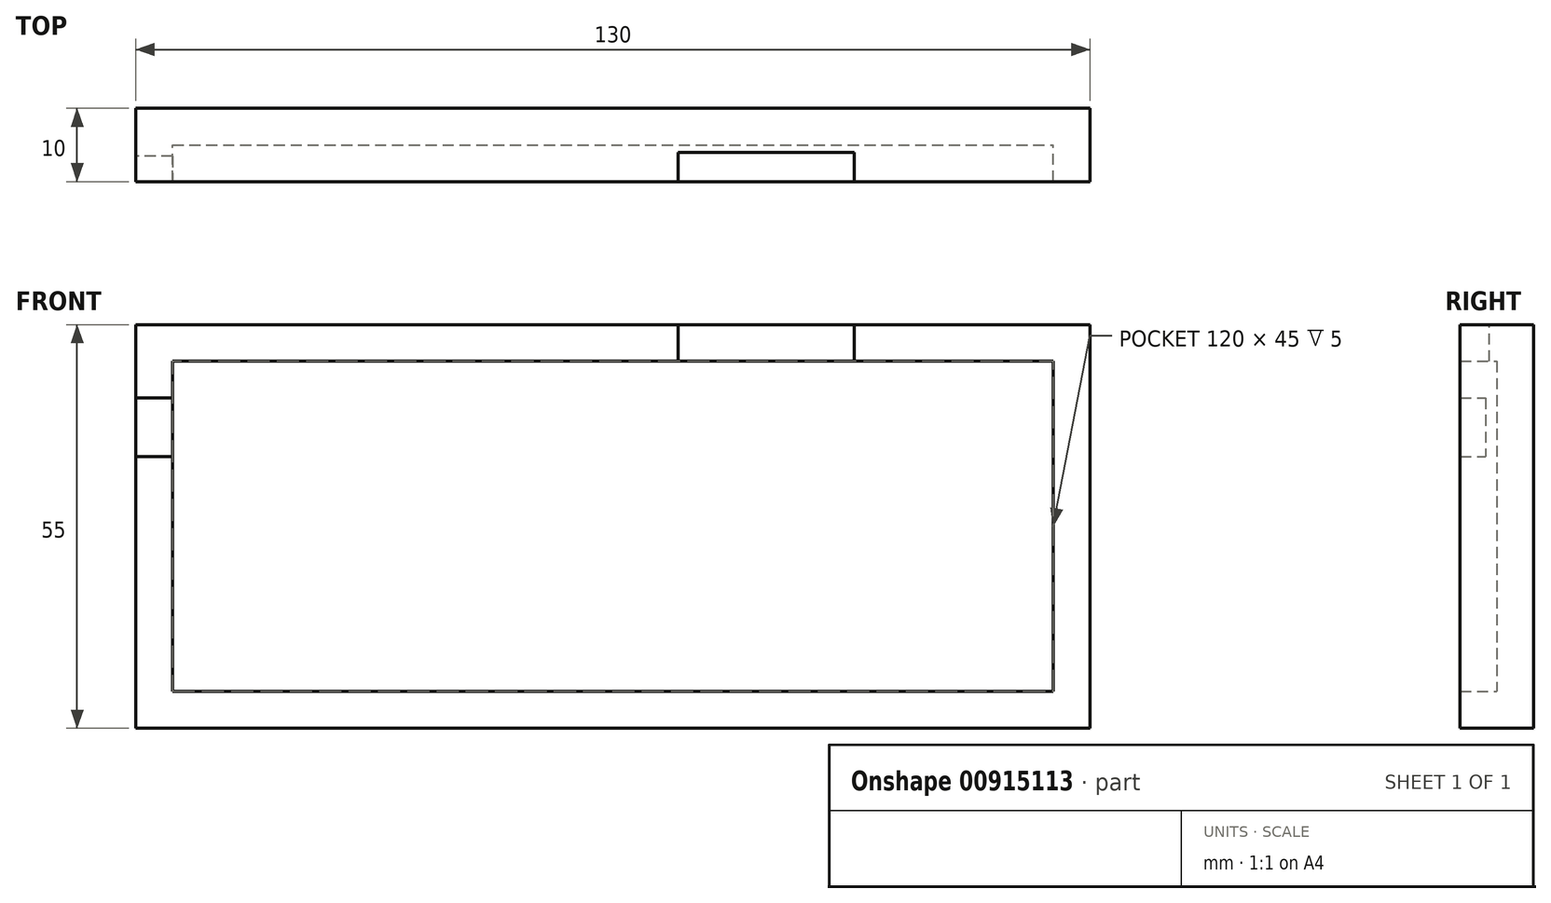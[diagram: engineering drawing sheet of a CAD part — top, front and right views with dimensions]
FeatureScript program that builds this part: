
annotation { "Feature Type Name" : "Feature", "Feature Type Description" : "" }
export const myFeature = defineFeature(function(context is Context, id is Id, definition is map)
    precondition{}
    {
        {
            var Q0;
            Q0=qCreatedBy(makeId("Front.planeOp"),FACE);
            var sketch = newSketch(context, id + "F0", { "sketchPlane" : qUnion([Q0])});
            skLineSegment(sketch, "E0.bottom", {"start": v(0, 0) * mm, "end": v(130, 0) * mm});
            skLineSegment(sketch, "E0.top", {"start": v(0, -55) * mm, "end": v(130, -55) * mm});
            skLineSegment(sketch, "E0.left", {"start": v(0, 0) * mm, "end": v(0, -55) * mm});
            skLineSegment(sketch, "E0.right", {"start": v(130, 0) * mm, "end": v(130, -55) * mm});
            skSolve(sketch);
        }
        {
            var Q0;
            Q0 = qSketchRegion(id + "F0", true);
            extrude(context, id + "F1", {"entities" : qUnion([Q0]), "depth" : 10 * mm, "offsetDistance" : 25.4 * mm});
        }
        {
            var Q0;
            Q0=makeQuery(id+"F1.opExtrude","CAP_FACE",FACE,{"disambiguationData":[OSD([sQuery(id+"F0.wireOp",EDGE,"E0.bottom"),sQuery(id+"F0.wireOp",EDGE,"E0.top"),sQuery(id+"F0.wireOp",EDGE,"E0.left"),sQuery(id+"F0.wireOp",EDGE,"E0.right")])],"isStart":false});
            shell(context, id + "F2", {"entities" : qUnion([Q0]), "thickness" : 5 * mm});
        }
        {
            var Q0;
            Q0=qCreatedBy(makeId("Top.planeOp"),FACE);
            var sketch = newSketch(context, id + "F3", { "sketchPlane" : qUnion([Q0])});
            skLineSegment(sketch, "E1.bottom", {"start": v(73.91, -10.01) * mm, "end": v(97.91, -10.01) * mm});
            skLineSegment(sketch, "E1.top", {"start": v(73.91, -6.01) * mm, "end": v(97.91, -6.01) * mm});
            skLineSegment(sketch, "E1.left", {"start": v(73.91, -10.01) * mm, "end": v(73.91, -6.01) * mm});
            skLineSegment(sketch, "E1.right", {"start": v(97.91, -10.01) * mm, "end": v(97.91, -6.01) * mm});
            skLineSegment(sketch, "E2", {"start": v(124.91, -10) * mm, "end": v(97.91, -10) * mm});
            skSolve(sketch);
        }
        {
            var Q0;
            Q0 = qSketchRegion(id + "F3", true);
            extrude(context, id + "F4", {"entities" : qUnion([Q0]), "operationType" : NewBodyOperationType.REMOVE, "oppositeDirection" : true, "depth" : 11.68 * mm, "offsetDistance" : 25.4 * mm});
        }
        {
            var Q0;
            Q0=qCreatedBy(makeId("Right.planeOp"),FACE);
            var sketch = newSketch(context, id + "F5", { "sketchPlane" : qUnion([Q0])});
            skLineSegment(sketch, "E3.bottom", {"start": v(-10.04, -10) * mm, "end": v(-6.54, -10) * mm});
            skLineSegment(sketch, "E3.top", {"start": v(-10.04, -18) * mm, "end": v(-6.54, -18) * mm});
            skLineSegment(sketch, "E3.left", {"start": v(-10.04, -10) * mm, "end": v(-10.04, -18) * mm});
            skLineSegment(sketch, "E3.right", {"start": v(-6.54, -10) * mm, "end": v(-6.54, -18) * mm});
            skLineSegment(sketch, "E4", {"start": v(-10.04, -10) * mm, "end": v(-10.04, -5) * mm});
            skSolve(sketch);
        }
        {
            var Q0;
            Q0 = qSketchRegion(id + "F5", true);
            extrude(context, id + "F6", {"entities" : qUnion([Q0]), "operationType" : NewBodyOperationType.REMOVE, "depth" : 6.78 * mm, "offsetDistance" : 25.4 * mm});
        }
    });
